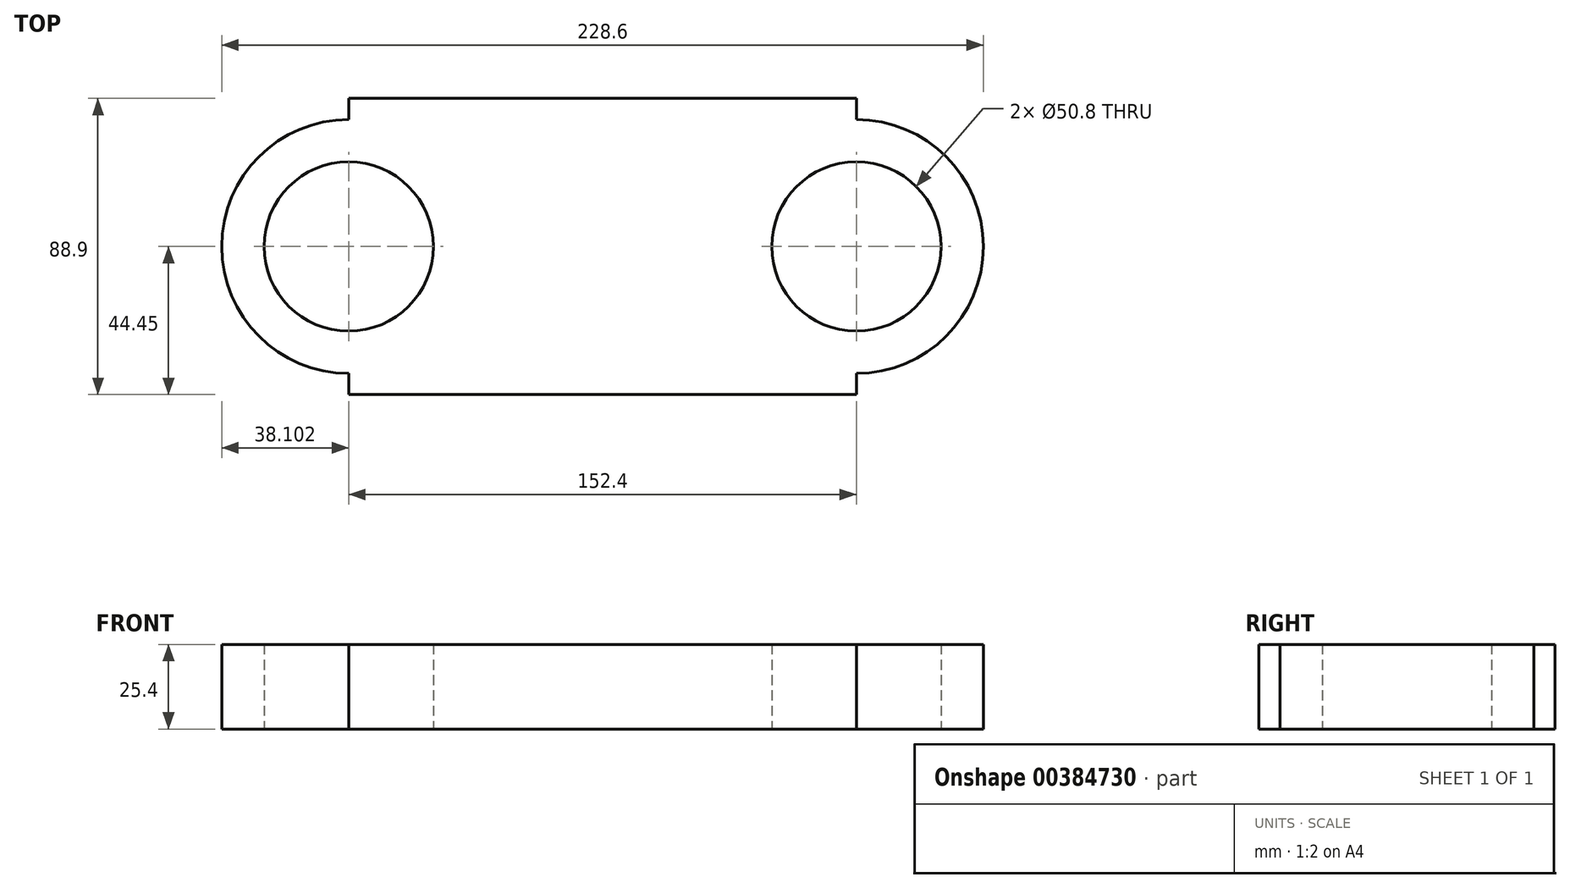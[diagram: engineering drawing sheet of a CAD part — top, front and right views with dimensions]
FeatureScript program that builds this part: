
annotation { "Feature Type Name" : "Feature", "Feature Type Description" : "" }
export const myFeature = defineFeature(function(context is Context, id is Id, definition is map)
    precondition{}
    {
        {
            var Q0;
            Q0=qCreatedBy(makeId("Top.planeOp"),FACE);
            var sketch = newSketch(context, id + "F0", { "sketchPlane" : qUnion([Q0])});
            skLineSegment(sketch, "E0.bottom", {"start": v(-75.67, 46.9) * mm, "end": v(76.73, 46.9) * mm});
            skLineSegment(sketch, "E0.top", {"start": v(-75.67, -42) * mm, "end": v(76.73, -42) * mm});
            skLineSegment(sketch, "E0.left", {"start": v(-75.67, 46.9) * mm, "end": v(-75.67, -42) * mm});
            skLineSegment(sketch, "E0.right", {"start": v(76.73, 46.9) * mm, "end": v(76.73, -42) * mm});
            skCircle(sketch, "E1", {"center": v(76.73, 2.44) * mm, "radius": 38.1 * mm});
            skCircle(sketch, "E2", {"center": v(76.73, 2.44) * mm, "radius": 25.4 * mm});
            skCircle(sketch, "E3", {"center": v(-75.67, 2.44) * mm, "radius": 38.1 * mm});
            skCircle(sketch, "E4", {"center": v(-75.67, 2.44) * mm, "radius": 25.4 * mm});
            skSolve(sketch);
        }
        {
            var Q0;
            {var subQ0=sQuery(id+"F0.wireOp",EDGE,"E3");var subQ1=sQuery(id+"F0.wireOp",EDGE,"E0.left");var subQ2=makeQuery(id+"F0.imprint","INTERSECT",VERTEX,{"disambiguationData":[OD(0.0)],"derivedFrom":[subQ1,subQ0]});Q0=makeQuery(id+"F0.imprint","IMPRINT",FACE,{"disambiguationData":[TD([[makeQuery(id+"F0.imprint","IMPRINT",EDGE,{"disambiguationData":[TD([[subQ2,-1.0]])],"derivedFrom":subQ1}),1.0]])]});}
            var Q1;
            {var subQ0=sQuery(id+"F0.wireOp",EDGE,"E1");var subQ1=sQuery(id+"F0.wireOp",EDGE,"E0.right");var subQ2=makeQuery(id+"F0.imprint","INTERSECT",VERTEX,{"disambiguationData":[OD(0.0)],"derivedFrom":[subQ1,subQ0]});Q1=makeQuery(id+"F0.imprint","IMPRINT",FACE,{"disambiguationData":[TD([[makeQuery(id+"F0.imprint","IMPRINT",EDGE,{"disambiguationData":[TD([[subQ2,-1.0]])],"derivedFrom":subQ1}),-1.0]])]});}
            var Q2;
            {var subQ1=sQuery(id+"F0.wireOp",EDGE,"E0.bottom");Q2=makeQuery(id+"F0.imprint","IMPRINT",FACE,{"disambiguationData":[TD([[makeQuery(id+"F0.imprint","IMPRINT",EDGE,{"derivedFrom":subQ1}),-1.0]])]});}
            var Q3;
            {var subQ0=sQuery(id+"F0.wireOp",EDGE,"E3");var subQ1=sQuery(id+"F0.wireOp",EDGE,"E0.left");var subQ2=makeQuery(id+"F0.imprint","INTERSECT",VERTEX,{"disambiguationData":[OD(0.0)],"derivedFrom":[subQ1,subQ0]});Q3=makeQuery(id+"F0.imprint","IMPRINT",FACE,{"disambiguationData":[TD([[makeQuery(id+"F0.imprint","IMPRINT",EDGE,{"disambiguationData":[TD([[subQ2,-1.0]])],"derivedFrom":subQ1}),-1.0]])]});}
            var Q4;
            {var subQ0=sQuery(id+"F0.wireOp",EDGE,"E1");var subQ1=sQuery(id+"F0.wireOp",EDGE,"E0.right");var subQ2=makeQuery(id+"F0.imprint","INTERSECT",VERTEX,{"disambiguationData":[OD(0.0)],"derivedFrom":[subQ1,subQ0]});Q4=makeQuery(id+"F0.imprint","IMPRINT",FACE,{"disambiguationData":[TD([[makeQuery(id+"F0.imprint","IMPRINT",EDGE,{"disambiguationData":[TD([[subQ2,-1.0]])],"derivedFrom":subQ1}),1.0]])]});}
            extrude(context, id + "F1", {"entities" : qUnion([Q0, Q1, Q2, Q3, Q4]), "depth" : 25.4 * mm});
        }
    });
